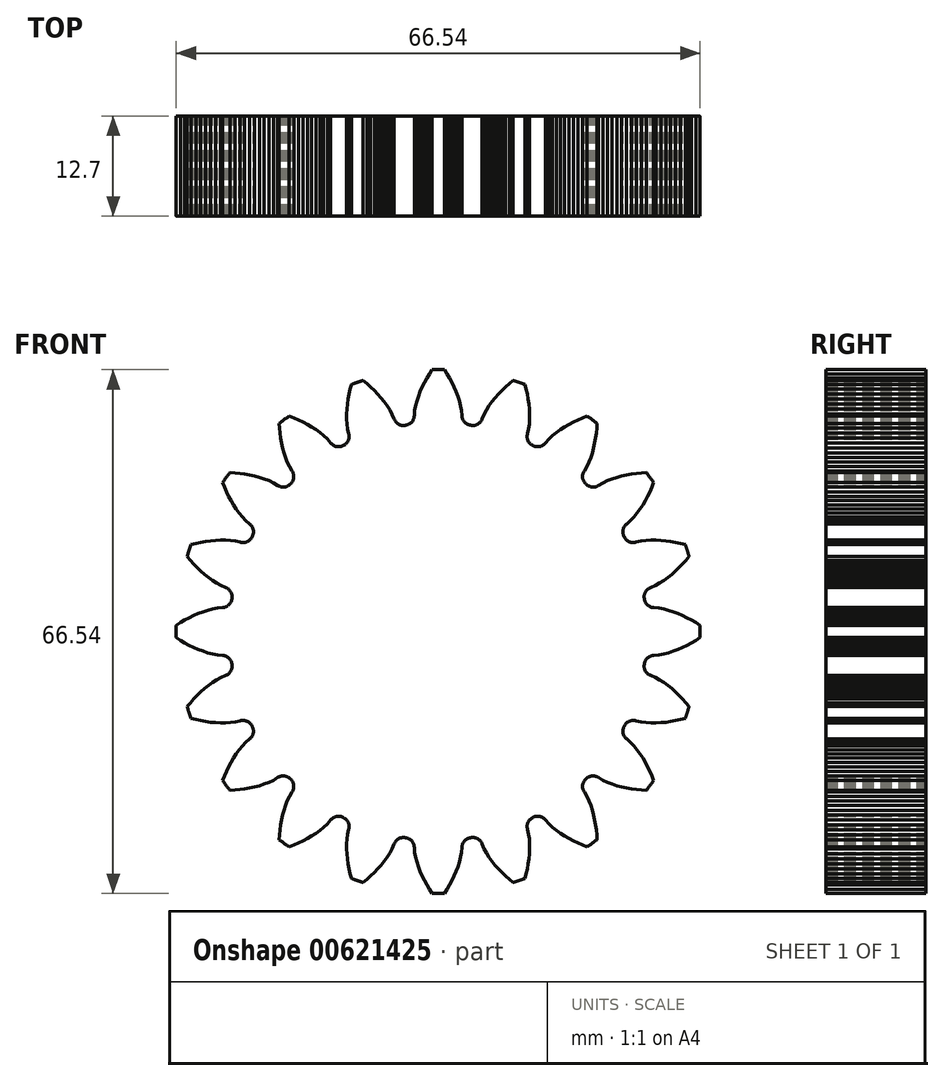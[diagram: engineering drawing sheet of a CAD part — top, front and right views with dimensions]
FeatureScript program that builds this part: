
annotation { "Feature Type Name" : "Feature", "Feature Type Description" : "" }
export const myFeature = defineFeature(function(context is Context, id is Id, definition is map)
    precondition{}
    {
        {
            var Q0;
            Q0=qCreatedBy(makeId("Front.planeOp"),FACE);
            var sketch = newSketch(context, id + "F0", { "sketchPlane" : qUnion([Q0])});
            skLineSegment(sketch, "E0", {"start": v(3.03, 27.4) * mm, "end": v(2.97, 28.04) * mm});
            skLineSegment(sketch, "E1", {"start": v(2.97, 28.04) * mm, "end": v(2.86, 28.66) * mm});
            skLineSegment(sketch, "E2", {"start": v(2.86, 28.66) * mm, "end": v(2.7, 29.28) * mm});
            skLineSegment(sketch, "E3", {"start": v(2.7, 29.28) * mm, "end": v(2.5, 29.88) * mm});
            skLineSegment(sketch, "E4", {"start": v(2.5, 29.88) * mm, "end": v(2.28, 30.47) * mm});
            skLineSegment(sketch, "E5", {"start": v(2.28, 30.47) * mm, "end": v(2.02, 31.05) * mm});
            skLineSegment(sketch, "E6", {"start": v(2.02, 31.05) * mm, "end": v(1.74, 31.62) * mm});
            skLineSegment(sketch, "E7", {"start": v(1.74, 31.62) * mm, "end": v(1.44, 32.18) * mm});
            skLineSegment(sketch, "E8", {"start": v(1.44, 32.18) * mm, "end": v(1.12, 32.73) * mm});
            skLineSegment(sketch, "E9", {"start": v(1.12, 32.73) * mm, "end": v(0.78, 33.26) * mm});
            skLineSegment(sketch, "E10", {"start": v(-3.03, 27.4) * mm, "end": v(-2.97, 28.04) * mm});
            skLineSegment(sketch, "E11", {"start": v(-2.97, 28.04) * mm, "end": v(-2.86, 28.66) * mm});
            skLineSegment(sketch, "E12", {"start": v(-2.86, 28.66) * mm, "end": v(-2.7, 29.28) * mm});
            skLineSegment(sketch, "E13", {"start": v(-2.7, 29.28) * mm, "end": v(-2.5, 29.88) * mm});
            skLineSegment(sketch, "E14", {"start": v(-2.5, 29.88) * mm, "end": v(-2.28, 30.47) * mm});
            skLineSegment(sketch, "E15", {"start": v(-2.28, 30.47) * mm, "end": v(-2.02, 31.05) * mm});
            skLineSegment(sketch, "E16", {"start": v(-2.02, 31.05) * mm, "end": v(-1.74, 31.62) * mm});
            skLineSegment(sketch, "E17", {"start": v(-1.74, 31.62) * mm, "end": v(-1.44, 32.18) * mm});
            skLineSegment(sketch, "E18", {"start": v(-1.44, 32.18) * mm, "end": v(-1.12, 32.73) * mm});
            skLineSegment(sketch, "E19", {"start": v(-1.12, 32.73) * mm, "end": v(-0.78, 33.26) * mm});
            skArc(sketch, "E20", {"start": v(-4.08, 26.2) * mm, "mid": v(-4.15, 26.2) * mm, "end": v(-4.22, 26.19) * mm});
            skArc(sketch, "E21", {"start": v(-4.08, 26.2) * mm, "mid": v(-3.34, 26.62) * mm, "end": v(-3.03, 27.4) * mm});
            skArc(sketch, "E22", {"start": v(3.03, 27.4) * mm, "mid": v(3.34, 26.62) * mm, "end": v(4.08, 26.2) * mm});
            skArc(sketch, "E23", {"start": v(0.78, 33.26) * mm, "mid": v(0, 33.27) * mm, "end": v(-0.78, 33.26) * mm});
            skArc(sketch, "E24", {"start": v(-11.98, 23.66) * mm, "mid": v(-12.04, 23.63) * mm, "end": v(-12.1, 23.6) * mm});
            skArc(sketch, "E25", {"start": v(-18.7, 18.8) * mm, "mid": v(-18.76, 18.76) * mm, "end": v(-18.8, 18.7) * mm});
            skArc(sketch, "E26", {"start": v(-23.6, 12.1) * mm, "mid": v(-23.63, 12.04) * mm, "end": v(-23.66, 11.98) * mm});
            skArc(sketch, "E27", {"start": v(-26.19, 4.22) * mm, "mid": v(-26.2, 4.15) * mm, "end": v(-26.2, 4.08) * mm});
            skArc(sketch, "E28", {"start": v(-26.2, -4.08) * mm, "mid": v(-26.2, -4.15) * mm, "end": v(-26.19, -4.22) * mm});
            skLineSegment(sketch, "E29", {"start": v(-5.59, 27) * mm, "end": v(-5.84, 27.59) * mm});
            skLineSegment(sketch, "E30", {"start": v(-5.84, 27.59) * mm, "end": v(-6.14, 28.14) * mm});
            skLineSegment(sketch, "E31", {"start": v(-6.14, 28.14) * mm, "end": v(-6.48, 28.68) * mm});
            skLineSegment(sketch, "E32", {"start": v(-6.48, 28.68) * mm, "end": v(-6.85, 29.2) * mm});
            skLineSegment(sketch, "E33", {"start": v(-6.85, 29.2) * mm, "end": v(-7.25, 29.69) * mm});
            skLineSegment(sketch, "E34", {"start": v(-7.25, 29.69) * mm, "end": v(-7.67, 30.16) * mm});
            skLineSegment(sketch, "E35", {"start": v(-7.67, 30.16) * mm, "end": v(-8.11, 30.62) * mm});
            skLineSegment(sketch, "E36", {"start": v(-8.11, 30.62) * mm, "end": v(-8.57, 31.05) * mm});
            skLineSegment(sketch, "E37", {"start": v(-8.57, 31.05) * mm, "end": v(-9.05, 31.47) * mm});
            skLineSegment(sketch, "E38", {"start": v(-9.05, 31.47) * mm, "end": v(-9.54, 31.88) * mm});
            skLineSegment(sketch, "E39", {"start": v(-13.66, 23.96) * mm, "end": v(-14.08, 24.43) * mm});
            skLineSegment(sketch, "E40", {"start": v(-14.08, 24.43) * mm, "end": v(-14.54, 24.87) * mm});
            skLineSegment(sketch, "E41", {"start": v(-14.54, 24.87) * mm, "end": v(-15.03, 25.27) * mm});
            skLineSegment(sketch, "E42", {"start": v(-15.03, 25.27) * mm, "end": v(-15.54, 25.65) * mm});
            skLineSegment(sketch, "E43", {"start": v(-15.54, 25.65) * mm, "end": v(-16.07, 26) * mm});
            skLineSegment(sketch, "E44", {"start": v(-16.07, 26) * mm, "end": v(-16.62, 26.31) * mm});
            skLineSegment(sketch, "E45", {"start": v(-16.62, 26.31) * mm, "end": v(-17.18, 26.61) * mm});
            skLineSegment(sketch, "E46", {"start": v(-17.18, 26.61) * mm, "end": v(-17.75, 26.89) * mm});
            skLineSegment(sketch, "E47", {"start": v(-17.75, 26.89) * mm, "end": v(-18.33, 27.14) * mm});
            skLineSegment(sketch, "E48", {"start": v(-18.33, 27.14) * mm, "end": v(-18.92, 27.37) * mm});
            skArc(sketch, "E49", {"start": v(-23.66, -11.98) * mm, "mid": v(-23.63, -12.04) * mm, "end": v(-23.6, -12.1) * mm});
            skArc(sketch, "E50", {"start": v(-18.8, -18.7) * mm, "mid": v(-18.76, -18.76) * mm, "end": v(-18.7, -18.8) * mm});
            skArc(sketch, "E51", {"start": v(-12.1, -23.6) * mm, "mid": v(-12.04, -23.63) * mm, "end": v(-11.98, -23.66) * mm});
            skArc(sketch, "E52", {"start": v(-4.22, -26.19) * mm, "mid": v(-4.15, -26.2) * mm, "end": v(-4.08, -26.2) * mm});
            skLineSegment(sketch, "E53", {"start": v(-20.4, 18.56) * mm, "end": v(-20.94, 18.89) * mm});
            skLineSegment(sketch, "E54", {"start": v(-20.94, 18.89) * mm, "end": v(-21.5, 19.16) * mm});
            skLineSegment(sketch, "E55", {"start": v(-21.5, 19.16) * mm, "end": v(-22.1, 19.4) * mm});
            skLineSegment(sketch, "E56", {"start": v(-22.1, 19.4) * mm, "end": v(-22.7, 19.59) * mm});
            skLineSegment(sketch, "E57", {"start": v(-22.7, 19.59) * mm, "end": v(-23.32, 19.75) * mm});
            skLineSegment(sketch, "E58", {"start": v(-23.32, 19.75) * mm, "end": v(-23.93, 19.89) * mm});
            skLineSegment(sketch, "E59", {"start": v(-23.93, 19.89) * mm, "end": v(-24.56, 20) * mm});
            skLineSegment(sketch, "E60", {"start": v(-24.56, 20) * mm, "end": v(-25.19, 20.08) * mm});
            skLineSegment(sketch, "E61", {"start": v(-25.19, 20.08) * mm, "end": v(-25.82, 20.15) * mm});
            skLineSegment(sketch, "E62", {"start": v(-25.82, 20.15) * mm, "end": v(-26.45, 20.19) * mm});
            skLineSegment(sketch, "E63", {"start": v(-25.13, 11.35) * mm, "end": v(-25.75, 11.5) * mm});
            skLineSegment(sketch, "E64", {"start": v(-25.75, 11.5) * mm, "end": v(-26.38, 11.58) * mm});
            skLineSegment(sketch, "E65", {"start": v(-26.38, 11.58) * mm, "end": v(-27.01, 11.61) * mm});
            skLineSegment(sketch, "E66", {"start": v(-27.01, 11.61) * mm, "end": v(-27.64, 11.61) * mm});
            skLineSegment(sketch, "E67", {"start": v(-27.64, 11.61) * mm, "end": v(-28.28, 11.58) * mm});
            skLineSegment(sketch, "E68", {"start": v(-28.28, 11.58) * mm, "end": v(-28.9, 11.52) * mm});
            skLineSegment(sketch, "E69", {"start": v(-28.9, 11.52) * mm, "end": v(-29.54, 11.43) * mm});
            skLineSegment(sketch, "E70", {"start": v(-29.54, 11.43) * mm, "end": v(-30.16, 11.32) * mm});
            skLineSegment(sketch, "E71", {"start": v(-30.16, 11.32) * mm, "end": v(-30.78, 11.18) * mm});
            skLineSegment(sketch, "E72", {"start": v(-30.78, 11.18) * mm, "end": v(-31.4, 11.02) * mm});
            skLineSegment(sketch, "E73", {"start": v(-27.4, 3.03) * mm, "end": v(-28.04, 2.97) * mm});
            skLineSegment(sketch, "E74", {"start": v(-28.04, 2.97) * mm, "end": v(-28.66, 2.86) * mm});
            skLineSegment(sketch, "E75", {"start": v(-28.66, 2.86) * mm, "end": v(-29.28, 2.7) * mm});
            skLineSegment(sketch, "E76", {"start": v(-29.28, 2.7) * mm, "end": v(-29.88, 2.5) * mm});
            skLineSegment(sketch, "E77", {"start": v(-29.88, 2.5) * mm, "end": v(-30.47, 2.28) * mm});
            skLineSegment(sketch, "E78", {"start": v(-30.47, 2.28) * mm, "end": v(-31.05, 2.02) * mm});
            skLineSegment(sketch, "E79", {"start": v(-31.05, 2.02) * mm, "end": v(-31.62, 1.74) * mm});
            skLineSegment(sketch, "E80", {"start": v(-31.62, 1.74) * mm, "end": v(-32.18, 1.44) * mm});
            skLineSegment(sketch, "E81", {"start": v(-32.18, 1.44) * mm, "end": v(-32.73, 1.12) * mm});
            skLineSegment(sketch, "E82", {"start": v(-32.73, 1.12) * mm, "end": v(-33.26, 0.78) * mm});
            skLineSegment(sketch, "E83", {"start": v(-27, -5.59) * mm, "end": v(-27.59, -5.84) * mm});
            skLineSegment(sketch, "E84", {"start": v(-27.59, -5.84) * mm, "end": v(-28.14, -6.14) * mm});
            skLineSegment(sketch, "E85", {"start": v(-28.14, -6.14) * mm, "end": v(-28.68, -6.48) * mm});
            skLineSegment(sketch, "E86", {"start": v(-28.68, -6.48) * mm, "end": v(-29.2, -6.85) * mm});
            skLineSegment(sketch, "E87", {"start": v(-29.2, -6.85) * mm, "end": v(-29.69, -7.25) * mm});
            skLineSegment(sketch, "E88", {"start": v(-29.69, -7.25) * mm, "end": v(-30.16, -7.67) * mm});
            skLineSegment(sketch, "E89", {"start": v(-30.16, -7.67) * mm, "end": v(-30.62, -8.11) * mm});
            skLineSegment(sketch, "E90", {"start": v(-30.62, -8.11) * mm, "end": v(-31.05, -8.57) * mm});
            skLineSegment(sketch, "E91", {"start": v(-31.05, -8.57) * mm, "end": v(-31.47, -9.05) * mm});
            skLineSegment(sketch, "E92", {"start": v(-31.47, -9.05) * mm, "end": v(-31.88, -9.54) * mm});
            skArc(sketch, "E93", {"start": v(4.08, -26.2) * mm, "mid": v(4.15, -26.2) * mm, "end": v(4.22, -26.19) * mm});
            skArc(sketch, "E94", {"start": v(11.98, -23.66) * mm, "mid": v(12.04, -23.63) * mm, "end": v(12.1, -23.6) * mm});
            skArc(sketch, "E95", {"start": v(18.7, -18.8) * mm, "mid": v(18.76, -18.76) * mm, "end": v(18.8, -18.7) * mm});
            skArc(sketch, "E96", {"start": v(23.6, -12.1) * mm, "mid": v(23.63, -12.04) * mm, "end": v(23.66, -11.98) * mm});
            skLineSegment(sketch, "E97", {"start": v(-23.96, -13.66) * mm, "end": v(-24.43, -14.08) * mm});
            skLineSegment(sketch, "E98", {"start": v(-24.43, -14.08) * mm, "end": v(-24.87, -14.54) * mm});
            skLineSegment(sketch, "E99", {"start": v(-24.87, -14.54) * mm, "end": v(-25.27, -15.03) * mm});
            skLineSegment(sketch, "E100", {"start": v(-25.27, -15.03) * mm, "end": v(-25.65, -15.54) * mm});
            skLineSegment(sketch, "E101", {"start": v(-25.65, -15.54) * mm, "end": v(-26, -16.07) * mm});
            skLineSegment(sketch, "E102", {"start": v(-26, -16.07) * mm, "end": v(-26.31, -16.62) * mm});
            skLineSegment(sketch, "E103", {"start": v(-26.31, -16.62) * mm, "end": v(-26.61, -17.18) * mm});
            skLineSegment(sketch, "E104", {"start": v(-26.61, -17.18) * mm, "end": v(-26.89, -17.75) * mm});
            skLineSegment(sketch, "E105", {"start": v(-26.89, -17.75) * mm, "end": v(-27.14, -18.33) * mm});
            skLineSegment(sketch, "E106", {"start": v(-27.14, -18.33) * mm, "end": v(-27.37, -18.92) * mm});
            skLineSegment(sketch, "E107", {"start": v(-18.56, -20.4) * mm, "end": v(-18.89, -20.94) * mm});
            skLineSegment(sketch, "E108", {"start": v(-18.89, -20.94) * mm, "end": v(-19.16, -21.5) * mm});
            skLineSegment(sketch, "E109", {"start": v(-19.16, -21.5) * mm, "end": v(-19.4, -22.1) * mm});
            skLineSegment(sketch, "E110", {"start": v(-19.4, -22.1) * mm, "end": v(-19.59, -22.7) * mm});
            skLineSegment(sketch, "E111", {"start": v(-19.59, -22.7) * mm, "end": v(-19.75, -23.32) * mm});
            skLineSegment(sketch, "E112", {"start": v(-19.75, -23.32) * mm, "end": v(-19.89, -23.93) * mm});
            skLineSegment(sketch, "E113", {"start": v(-19.89, -23.93) * mm, "end": v(-20, -24.56) * mm});
            skLineSegment(sketch, "E114", {"start": v(-20, -24.56) * mm, "end": v(-20.08, -25.19) * mm});
            skLineSegment(sketch, "E115", {"start": v(-20.08, -25.19) * mm, "end": v(-20.15, -25.82) * mm});
            skLineSegment(sketch, "E116", {"start": v(-20.15, -25.82) * mm, "end": v(-20.19, -26.45) * mm});
            skLineSegment(sketch, "E117", {"start": v(-11.35, -25.13) * mm, "end": v(-11.5, -25.75) * mm});
            skLineSegment(sketch, "E118", {"start": v(-11.5, -25.75) * mm, "end": v(-11.58, -26.38) * mm});
            skLineSegment(sketch, "E119", {"start": v(-11.58, -26.38) * mm, "end": v(-11.61, -27.01) * mm});
            skLineSegment(sketch, "E120", {"start": v(-11.61, -27.01) * mm, "end": v(-11.61, -27.64) * mm});
            skLineSegment(sketch, "E121", {"start": v(-11.61, -27.64) * mm, "end": v(-11.58, -28.28) * mm});
            skLineSegment(sketch, "E122", {"start": v(-11.58, -28.28) * mm, "end": v(-11.52, -28.9) * mm});
            skLineSegment(sketch, "E123", {"start": v(-11.52, -28.9) * mm, "end": v(-11.43, -29.54) * mm});
            skLineSegment(sketch, "E124", {"start": v(-11.43, -29.54) * mm, "end": v(-11.32, -30.16) * mm});
            skLineSegment(sketch, "E125", {"start": v(-11.32, -30.16) * mm, "end": v(-11.18, -30.78) * mm});
            skLineSegment(sketch, "E126", {"start": v(-11.18, -30.78) * mm, "end": v(-11.02, -31.4) * mm});
            skLineSegment(sketch, "E127", {"start": v(-3.03, -27.4) * mm, "end": v(-2.97, -28.04) * mm});
            skLineSegment(sketch, "E128", {"start": v(-2.97, -28.04) * mm, "end": v(-2.86, -28.66) * mm});
            skLineSegment(sketch, "E129", {"start": v(-2.86, -28.66) * mm, "end": v(-2.7, -29.28) * mm});
            skLineSegment(sketch, "E130", {"start": v(-2.7, -29.28) * mm, "end": v(-2.5, -29.88) * mm});
            skLineSegment(sketch, "E131", {"start": v(-2.5, -29.88) * mm, "end": v(-2.28, -30.47) * mm});
            skLineSegment(sketch, "E132", {"start": v(-2.28, -30.47) * mm, "end": v(-2.02, -31.05) * mm});
            skLineSegment(sketch, "E133", {"start": v(-2.02, -31.05) * mm, "end": v(-1.74, -31.62) * mm});
            skLineSegment(sketch, "E134", {"start": v(-1.74, -31.62) * mm, "end": v(-1.44, -32.18) * mm});
            skLineSegment(sketch, "E135", {"start": v(-1.44, -32.18) * mm, "end": v(-1.12, -32.73) * mm});
            skLineSegment(sketch, "E136", {"start": v(-1.12, -32.73) * mm, "end": v(-0.78, -33.26) * mm});
            skArc(sketch, "E137", {"start": v(26.19, -4.22) * mm, "mid": v(26.2, -4.15) * mm, "end": v(26.2, -4.08) * mm});
            skArc(sketch, "E138", {"start": v(26.2, 4.08) * mm, "mid": v(26.2, 4.15) * mm, "end": v(26.19, 4.22) * mm});
            skArc(sketch, "E139", {"start": v(23.66, 11.98) * mm, "mid": v(23.63, 12.04) * mm, "end": v(23.6, 12.1) * mm});
            skArc(sketch, "E140", {"start": v(18.8, 18.7) * mm, "mid": v(18.76, 18.76) * mm, "end": v(18.7, 18.8) * mm});
            skLineSegment(sketch, "E141", {"start": v(5.59, -27) * mm, "end": v(5.84, -27.59) * mm});
            skLineSegment(sketch, "E142", {"start": v(5.84, -27.59) * mm, "end": v(6.14, -28.14) * mm});
            skLineSegment(sketch, "E143", {"start": v(6.14, -28.14) * mm, "end": v(6.48, -28.68) * mm});
            skLineSegment(sketch, "E144", {"start": v(6.48, -28.68) * mm, "end": v(6.85, -29.2) * mm});
            skLineSegment(sketch, "E145", {"start": v(6.85, -29.2) * mm, "end": v(7.25, -29.69) * mm});
            skLineSegment(sketch, "E146", {"start": v(7.25, -29.69) * mm, "end": v(7.67, -30.16) * mm});
            skLineSegment(sketch, "E147", {"start": v(7.67, -30.16) * mm, "end": v(8.11, -30.62) * mm});
            skLineSegment(sketch, "E148", {"start": v(8.11, -30.62) * mm, "end": v(8.57, -31.05) * mm});
            skLineSegment(sketch, "E149", {"start": v(8.57, -31.05) * mm, "end": v(9.05, -31.47) * mm});
            skLineSegment(sketch, "E150", {"start": v(9.05, -31.47) * mm, "end": v(9.54, -31.88) * mm});
            skLineSegment(sketch, "E151", {"start": v(13.66, -23.96) * mm, "end": v(14.08, -24.43) * mm});
            skLineSegment(sketch, "E152", {"start": v(14.08, -24.43) * mm, "end": v(14.54, -24.87) * mm});
            skLineSegment(sketch, "E153", {"start": v(14.54, -24.87) * mm, "end": v(15.03, -25.27) * mm});
            skLineSegment(sketch, "E154", {"start": v(15.03, -25.27) * mm, "end": v(15.54, -25.65) * mm});
            skLineSegment(sketch, "E155", {"start": v(15.54, -25.65) * mm, "end": v(16.07, -26) * mm});
            skLineSegment(sketch, "E156", {"start": v(16.07, -26) * mm, "end": v(16.62, -26.31) * mm});
            skLineSegment(sketch, "E157", {"start": v(16.62, -26.31) * mm, "end": v(17.18, -26.61) * mm});
            skLineSegment(sketch, "E158", {"start": v(17.18, -26.61) * mm, "end": v(17.75, -26.89) * mm});
            skLineSegment(sketch, "E159", {"start": v(17.75, -26.89) * mm, "end": v(18.33, -27.14) * mm});
            skLineSegment(sketch, "E160", {"start": v(18.33, -27.14) * mm, "end": v(18.92, -27.37) * mm});
            skLineSegment(sketch, "E161", {"start": v(20.4, -18.56) * mm, "end": v(20.94, -18.89) * mm});
            skLineSegment(sketch, "E162", {"start": v(20.94, -18.89) * mm, "end": v(21.5, -19.16) * mm});
            skLineSegment(sketch, "E163", {"start": v(21.5, -19.16) * mm, "end": v(22.1, -19.4) * mm});
            skLineSegment(sketch, "E164", {"start": v(22.1, -19.4) * mm, "end": v(22.7, -19.59) * mm});
            skLineSegment(sketch, "E165", {"start": v(22.7, -19.59) * mm, "end": v(23.32, -19.75) * mm});
            skLineSegment(sketch, "E166", {"start": v(23.32, -19.75) * mm, "end": v(23.93, -19.89) * mm});
            skLineSegment(sketch, "E167", {"start": v(23.93, -19.89) * mm, "end": v(24.56, -20) * mm});
            skLineSegment(sketch, "E168", {"start": v(24.56, -20) * mm, "end": v(25.19, -20.08) * mm});
            skLineSegment(sketch, "E169", {"start": v(25.19, -20.08) * mm, "end": v(25.82, -20.15) * mm});
            skLineSegment(sketch, "E170", {"start": v(25.82, -20.15) * mm, "end": v(26.45, -20.19) * mm});
            skLineSegment(sketch, "E171", {"start": v(25.13, -11.35) * mm, "end": v(25.75, -11.5) * mm});
            skLineSegment(sketch, "E172", {"start": v(25.75, -11.5) * mm, "end": v(26.38, -11.58) * mm});
            skLineSegment(sketch, "E173", {"start": v(26.38, -11.58) * mm, "end": v(27.01, -11.61) * mm});
            skLineSegment(sketch, "E174", {"start": v(27.01, -11.61) * mm, "end": v(27.64, -11.61) * mm});
            skLineSegment(sketch, "E175", {"start": v(27.64, -11.61) * mm, "end": v(28.28, -11.58) * mm});
            skLineSegment(sketch, "E176", {"start": v(28.28, -11.58) * mm, "end": v(28.9, -11.52) * mm});
            skLineSegment(sketch, "E177", {"start": v(28.9, -11.52) * mm, "end": v(29.54, -11.43) * mm});
            skLineSegment(sketch, "E178", {"start": v(29.54, -11.43) * mm, "end": v(30.16, -11.32) * mm});
            skLineSegment(sketch, "E179", {"start": v(30.16, -11.32) * mm, "end": v(30.78, -11.18) * mm});
            skLineSegment(sketch, "E180", {"start": v(30.78, -11.18) * mm, "end": v(31.4, -11.02) * mm});
            skArc(sketch, "E181", {"start": v(12.1, 23.6) * mm, "mid": v(12.04, 23.63) * mm, "end": v(11.98, 23.66) * mm});
            skArc(sketch, "E182", {"start": v(4.22, 26.19) * mm, "mid": v(4.15, 26.2) * mm, "end": v(4.08, 26.2) * mm});
            skArc(sketch, "E183", {"start": v(-11.98, 23.66) * mm, "mid": v(-11.4, 24.28) * mm, "end": v(-11.35, 25.13) * mm});
            skArc(sketch, "E184", {"start": v(-18.7, 18.8) * mm, "mid": v(-18.35, 19.57) * mm, "end": v(-18.56, 20.4) * mm});
            skLineSegment(sketch, "E185", {"start": v(27.4, -3.03) * mm, "end": v(28.04, -2.97) * mm});
            skLineSegment(sketch, "E186", {"start": v(28.04, -2.97) * mm, "end": v(28.66, -2.86) * mm});
            skLineSegment(sketch, "E187", {"start": v(28.66, -2.86) * mm, "end": v(29.28, -2.7) * mm});
            skLineSegment(sketch, "E188", {"start": v(29.28, -2.7) * mm, "end": v(29.88, -2.5) * mm});
            skLineSegment(sketch, "E189", {"start": v(29.88, -2.5) * mm, "end": v(30.47, -2.28) * mm});
            skLineSegment(sketch, "E190", {"start": v(30.47, -2.28) * mm, "end": v(31.05, -2.02) * mm});
            skLineSegment(sketch, "E191", {"start": v(31.05, -2.02) * mm, "end": v(31.62, -1.74) * mm});
            skLineSegment(sketch, "E192", {"start": v(31.62, -1.74) * mm, "end": v(32.18, -1.44) * mm});
            skLineSegment(sketch, "E193", {"start": v(32.18, -1.44) * mm, "end": v(32.73, -1.12) * mm});
            skLineSegment(sketch, "E194", {"start": v(32.73, -1.12) * mm, "end": v(33.26, -0.78) * mm});
            skLineSegment(sketch, "E195", {"start": v(27, 5.59) * mm, "end": v(27.59, 5.84) * mm});
            skLineSegment(sketch, "E196", {"start": v(27.59, 5.84) * mm, "end": v(28.14, 6.14) * mm});
            skLineSegment(sketch, "E197", {"start": v(28.14, 6.14) * mm, "end": v(28.68, 6.48) * mm});
            skLineSegment(sketch, "E198", {"start": v(28.68, 6.48) * mm, "end": v(29.2, 6.85) * mm});
            skLineSegment(sketch, "E199", {"start": v(29.2, 6.85) * mm, "end": v(29.69, 7.25) * mm});
            skLineSegment(sketch, "E200", {"start": v(29.69, 7.25) * mm, "end": v(30.16, 7.67) * mm});
            skLineSegment(sketch, "E201", {"start": v(30.16, 7.67) * mm, "end": v(30.62, 8.11) * mm});
            skLineSegment(sketch, "E202", {"start": v(30.62, 8.11) * mm, "end": v(31.05, 8.57) * mm});
            skLineSegment(sketch, "E203", {"start": v(31.05, 8.57) * mm, "end": v(31.47, 9.05) * mm});
            skLineSegment(sketch, "E204", {"start": v(31.47, 9.05) * mm, "end": v(31.88, 9.54) * mm});
            skLineSegment(sketch, "E205", {"start": v(23.96, 13.66) * mm, "end": v(24.43, 14.08) * mm});
            skLineSegment(sketch, "E206", {"start": v(24.43, 14.08) * mm, "end": v(24.87, 14.54) * mm});
            skLineSegment(sketch, "E207", {"start": v(24.87, 14.54) * mm, "end": v(25.27, 15.03) * mm});
            skLineSegment(sketch, "E208", {"start": v(25.27, 15.03) * mm, "end": v(25.65, 15.54) * mm});
            skLineSegment(sketch, "E209", {"start": v(25.65, 15.54) * mm, "end": v(26, 16.07) * mm});
            skLineSegment(sketch, "E210", {"start": v(26, 16.07) * mm, "end": v(26.31, 16.62) * mm});
            skLineSegment(sketch, "E211", {"start": v(26.31, 16.62) * mm, "end": v(26.61, 17.18) * mm});
            skLineSegment(sketch, "E212", {"start": v(26.61, 17.18) * mm, "end": v(26.89, 17.75) * mm});
            skLineSegment(sketch, "E213", {"start": v(26.89, 17.75) * mm, "end": v(27.14, 18.33) * mm});
            skLineSegment(sketch, "E214", {"start": v(27.14, 18.33) * mm, "end": v(27.37, 18.92) * mm});
            skLineSegment(sketch, "E215", {"start": v(18.56, 20.4) * mm, "end": v(18.89, 20.94) * mm});
            skLineSegment(sketch, "E216", {"start": v(18.89, 20.94) * mm, "end": v(19.16, 21.5) * mm});
            skLineSegment(sketch, "E217", {"start": v(19.16, 21.5) * mm, "end": v(19.4, 22.1) * mm});
            skLineSegment(sketch, "E218", {"start": v(19.4, 22.1) * mm, "end": v(19.59, 22.7) * mm});
            skLineSegment(sketch, "E219", {"start": v(19.59, 22.7) * mm, "end": v(19.75, 23.32) * mm});
            skLineSegment(sketch, "E220", {"start": v(19.75, 23.32) * mm, "end": v(19.89, 23.93) * mm});
            skLineSegment(sketch, "E221", {"start": v(19.89, 23.93) * mm, "end": v(20, 24.56) * mm});
            skLineSegment(sketch, "E222", {"start": v(20, 24.56) * mm, "end": v(20.08, 25.19) * mm});
            skLineSegment(sketch, "E223", {"start": v(20.08, 25.19) * mm, "end": v(20.15, 25.82) * mm});
            skLineSegment(sketch, "E224", {"start": v(20.15, 25.82) * mm, "end": v(20.19, 26.45) * mm});
            skArc(sketch, "E225", {"start": v(-23.6, 12.1) * mm, "mid": v(-23.5, 12.94) * mm, "end": v(-23.96, 13.66) * mm});
            skArc(sketch, "E226", {"start": v(-26.19, 4.22) * mm, "mid": v(-26.35, 5.05) * mm, "end": v(-27, 5.59) * mm});
            skArc(sketch, "E227", {"start": v(-26.2, -4.08) * mm, "mid": v(-26.62, -3.34) * mm, "end": v(-27.4, -3.03) * mm});
            skArc(sketch, "E228", {"start": v(-23.66, -11.98) * mm, "mid": v(-24.28, -11.4) * mm, "end": v(-25.13, -11.35) * mm});
            skLineSegment(sketch, "E229", {"start": v(11.35, 25.13) * mm, "end": v(11.5, 25.75) * mm});
            skLineSegment(sketch, "E230", {"start": v(11.5, 25.75) * mm, "end": v(11.58, 26.38) * mm});
            skLineSegment(sketch, "E231", {"start": v(11.58, 26.38) * mm, "end": v(11.61, 27.01) * mm});
            skLineSegment(sketch, "E232", {"start": v(11.61, 27.01) * mm, "end": v(11.61, 27.64) * mm});
            skLineSegment(sketch, "E233", {"start": v(11.61, 27.64) * mm, "end": v(11.58, 28.28) * mm});
            skLineSegment(sketch, "E234", {"start": v(11.58, 28.28) * mm, "end": v(11.52, 28.9) * mm});
            skLineSegment(sketch, "E235", {"start": v(11.52, 28.9) * mm, "end": v(11.43, 29.54) * mm});
            skLineSegment(sketch, "E236", {"start": v(11.43, 29.54) * mm, "end": v(11.32, 30.16) * mm});
            skLineSegment(sketch, "E237", {"start": v(11.32, 30.16) * mm, "end": v(11.18, 30.78) * mm});
            skLineSegment(sketch, "E238", {"start": v(11.18, 30.78) * mm, "end": v(11.02, 31.4) * mm});
            skLineSegment(sketch, "E239", {"start": v(-11.35, 25.13) * mm, "end": v(-11.5, 25.75) * mm});
            skLineSegment(sketch, "E240", {"start": v(-11.5, 25.75) * mm, "end": v(-11.58, 26.38) * mm});
            skLineSegment(sketch, "E241", {"start": v(-11.58, 26.38) * mm, "end": v(-11.61, 27.01) * mm});
            skLineSegment(sketch, "E242", {"start": v(-11.61, 27.01) * mm, "end": v(-11.61, 27.64) * mm});
            skLineSegment(sketch, "E243", {"start": v(-11.61, 27.64) * mm, "end": v(-11.58, 28.28) * mm});
            skLineSegment(sketch, "E244", {"start": v(-11.58, 28.28) * mm, "end": v(-11.52, 28.9) * mm});
            skLineSegment(sketch, "E245", {"start": v(-11.52, 28.9) * mm, "end": v(-11.43, 29.54) * mm});
            skLineSegment(sketch, "E246", {"start": v(-11.43, 29.54) * mm, "end": v(-11.32, 30.16) * mm});
            skLineSegment(sketch, "E247", {"start": v(-11.32, 30.16) * mm, "end": v(-11.18, 30.78) * mm});
            skLineSegment(sketch, "E248", {"start": v(-11.18, 30.78) * mm, "end": v(-11.02, 31.4) * mm});
            skLineSegment(sketch, "E249", {"start": v(-18.56, 20.4) * mm, "end": v(-18.89, 20.94) * mm});
            skLineSegment(sketch, "E250", {"start": v(-18.89, 20.94) * mm, "end": v(-19.16, 21.5) * mm});
            skLineSegment(sketch, "E251", {"start": v(-19.16, 21.5) * mm, "end": v(-19.4, 22.1) * mm});
            skLineSegment(sketch, "E252", {"start": v(-19.4, 22.1) * mm, "end": v(-19.59, 22.7) * mm});
            skLineSegment(sketch, "E253", {"start": v(-19.59, 22.7) * mm, "end": v(-19.75, 23.32) * mm});
            skLineSegment(sketch, "E254", {"start": v(-19.75, 23.32) * mm, "end": v(-19.89, 23.93) * mm});
            skLineSegment(sketch, "E255", {"start": v(-19.89, 23.93) * mm, "end": v(-20, 24.56) * mm});
            skLineSegment(sketch, "E256", {"start": v(-20, 24.56) * mm, "end": v(-20.08, 25.19) * mm});
            skLineSegment(sketch, "E257", {"start": v(-20.08, 25.19) * mm, "end": v(-20.15, 25.82) * mm});
            skLineSegment(sketch, "E258", {"start": v(-20.15, 25.82) * mm, "end": v(-20.19, 26.45) * mm});
            skLineSegment(sketch, "E259", {"start": v(-23.96, 13.66) * mm, "end": v(-24.43, 14.08) * mm});
            skLineSegment(sketch, "E260", {"start": v(-24.43, 14.08) * mm, "end": v(-24.87, 14.54) * mm});
            skLineSegment(sketch, "E261", {"start": v(-24.87, 14.54) * mm, "end": v(-25.27, 15.03) * mm});
            skLineSegment(sketch, "E262", {"start": v(-25.27, 15.03) * mm, "end": v(-25.65, 15.54) * mm});
            skLineSegment(sketch, "E263", {"start": v(-25.65, 15.54) * mm, "end": v(-26, 16.07) * mm});
            skLineSegment(sketch, "E264", {"start": v(-26, 16.07) * mm, "end": v(-26.31, 16.62) * mm});
            skLineSegment(sketch, "E265", {"start": v(-26.31, 16.62) * mm, "end": v(-26.61, 17.18) * mm});
            skLineSegment(sketch, "E266", {"start": v(-26.61, 17.18) * mm, "end": v(-26.89, 17.75) * mm});
            skLineSegment(sketch, "E267", {"start": v(-26.89, 17.75) * mm, "end": v(-27.14, 18.33) * mm});
            skLineSegment(sketch, "E268", {"start": v(-27.14, 18.33) * mm, "end": v(-27.37, 18.92) * mm});
            skArc(sketch, "E269", {"start": v(-18.8, -18.7) * mm, "mid": v(-19.57, -18.35) * mm, "end": v(-20.4, -18.56) * mm});
            skArc(sketch, "E270", {"start": v(-12.1, -23.6) * mm, "mid": v(-12.94, -23.5) * mm, "end": v(-13.66, -23.96) * mm});
            skArc(sketch, "E271", {"start": v(-4.22, -26.19) * mm, "mid": v(-5.05, -26.35) * mm, "end": v(-5.59, -27) * mm});
            skArc(sketch, "E272", {"start": v(4.08, -26.2) * mm, "mid": v(3.34, -26.62) * mm, "end": v(3.03, -27.4) * mm});
            skLineSegment(sketch, "E273", {"start": v(-27, 5.59) * mm, "end": v(-27.59, 5.84) * mm});
            skLineSegment(sketch, "E274", {"start": v(-27.59, 5.84) * mm, "end": v(-28.14, 6.14) * mm});
            skLineSegment(sketch, "E275", {"start": v(-28.14, 6.14) * mm, "end": v(-28.68, 6.48) * mm});
            skLineSegment(sketch, "E276", {"start": v(-28.68, 6.48) * mm, "end": v(-29.2, 6.85) * mm});
            skLineSegment(sketch, "E277", {"start": v(-29.2, 6.85) * mm, "end": v(-29.69, 7.25) * mm});
            skLineSegment(sketch, "E278", {"start": v(-29.69, 7.25) * mm, "end": v(-30.16, 7.67) * mm});
            skLineSegment(sketch, "E279", {"start": v(-30.16, 7.67) * mm, "end": v(-30.62, 8.11) * mm});
            skLineSegment(sketch, "E280", {"start": v(-30.62, 8.11) * mm, "end": v(-31.05, 8.57) * mm});
            skLineSegment(sketch, "E281", {"start": v(-31.05, 8.57) * mm, "end": v(-31.47, 9.05) * mm});
            skLineSegment(sketch, "E282", {"start": v(-31.47, 9.05) * mm, "end": v(-31.88, 9.54) * mm});
            skLineSegment(sketch, "E283", {"start": v(-27.4, -3.03) * mm, "end": v(-28.04, -2.97) * mm});
            skLineSegment(sketch, "E284", {"start": v(-28.04, -2.97) * mm, "end": v(-28.66, -2.86) * mm});
            skLineSegment(sketch, "E285", {"start": v(-28.66, -2.86) * mm, "end": v(-29.28, -2.7) * mm});
            skLineSegment(sketch, "E286", {"start": v(-29.28, -2.7) * mm, "end": v(-29.88, -2.5) * mm});
            skLineSegment(sketch, "E287", {"start": v(-29.88, -2.5) * mm, "end": v(-30.47, -2.28) * mm});
            skLineSegment(sketch, "E288", {"start": v(-30.47, -2.28) * mm, "end": v(-31.05, -2.02) * mm});
            skLineSegment(sketch, "E289", {"start": v(-31.05, -2.02) * mm, "end": v(-31.62, -1.74) * mm});
            skLineSegment(sketch, "E290", {"start": v(-31.62, -1.74) * mm, "end": v(-32.18, -1.44) * mm});
            skLineSegment(sketch, "E291", {"start": v(-32.18, -1.44) * mm, "end": v(-32.73, -1.12) * mm});
            skLineSegment(sketch, "E292", {"start": v(-32.73, -1.12) * mm, "end": v(-33.26, -0.78) * mm});
            skLineSegment(sketch, "E293", {"start": v(-25.13, -11.35) * mm, "end": v(-25.75, -11.5) * mm});
            skLineSegment(sketch, "E294", {"start": v(-25.75, -11.5) * mm, "end": v(-26.38, -11.58) * mm});
            skLineSegment(sketch, "E295", {"start": v(-26.38, -11.58) * mm, "end": v(-27.01, -11.61) * mm});
            skLineSegment(sketch, "E296", {"start": v(-27.01, -11.61) * mm, "end": v(-27.64, -11.61) * mm});
            skLineSegment(sketch, "E297", {"start": v(-27.64, -11.61) * mm, "end": v(-28.28, -11.58) * mm});
            skLineSegment(sketch, "E298", {"start": v(-28.28, -11.58) * mm, "end": v(-28.9, -11.52) * mm});
            skLineSegment(sketch, "E299", {"start": v(-28.9, -11.52) * mm, "end": v(-29.54, -11.43) * mm});
            skLineSegment(sketch, "E300", {"start": v(-29.54, -11.43) * mm, "end": v(-30.16, -11.32) * mm});
            skLineSegment(sketch, "E301", {"start": v(-30.16, -11.32) * mm, "end": v(-30.78, -11.18) * mm});
            skLineSegment(sketch, "E302", {"start": v(-30.78, -11.18) * mm, "end": v(-31.4, -11.02) * mm});
            skLineSegment(sketch, "E303", {"start": v(-20.4, -18.56) * mm, "end": v(-20.94, -18.89) * mm});
            skLineSegment(sketch, "E304", {"start": v(-20.94, -18.89) * mm, "end": v(-21.5, -19.16) * mm});
            skLineSegment(sketch, "E305", {"start": v(-21.5, -19.16) * mm, "end": v(-22.1, -19.4) * mm});
            skLineSegment(sketch, "E306", {"start": v(-22.1, -19.4) * mm, "end": v(-22.7, -19.59) * mm});
            skLineSegment(sketch, "E307", {"start": v(-22.7, -19.59) * mm, "end": v(-23.32, -19.75) * mm});
            skLineSegment(sketch, "E308", {"start": v(-23.32, -19.75) * mm, "end": v(-23.93, -19.89) * mm});
            skLineSegment(sketch, "E309", {"start": v(-23.93, -19.89) * mm, "end": v(-24.56, -20) * mm});
            skLineSegment(sketch, "E310", {"start": v(-24.56, -20) * mm, "end": v(-25.19, -20.08) * mm});
            skLineSegment(sketch, "E311", {"start": v(-25.19, -20.08) * mm, "end": v(-25.82, -20.15) * mm});
            skLineSegment(sketch, "E312", {"start": v(-25.82, -20.15) * mm, "end": v(-26.45, -20.19) * mm});
            skArc(sketch, "E313", {"start": v(11.98, -23.66) * mm, "mid": v(11.4, -24.28) * mm, "end": v(11.35, -25.13) * mm});
            skArc(sketch, "E314", {"start": v(18.7, -18.8) * mm, "mid": v(18.35, -19.57) * mm, "end": v(18.56, -20.4) * mm});
            skArc(sketch, "E315", {"start": v(23.6, -12.1) * mm, "mid": v(23.5, -12.94) * mm, "end": v(23.96, -13.66) * mm});
            skArc(sketch, "E316", {"start": v(26.19, -4.22) * mm, "mid": v(26.35, -5.05) * mm, "end": v(27, -5.59) * mm});
            skLineSegment(sketch, "E317", {"start": v(-13.66, -23.96) * mm, "end": v(-14.08, -24.43) * mm});
            skLineSegment(sketch, "E318", {"start": v(-14.08, -24.43) * mm, "end": v(-14.54, -24.87) * mm});
            skLineSegment(sketch, "E319", {"start": v(-14.54, -24.87) * mm, "end": v(-15.03, -25.27) * mm});
            skLineSegment(sketch, "E320", {"start": v(-15.03, -25.27) * mm, "end": v(-15.54, -25.65) * mm});
            skLineSegment(sketch, "E321", {"start": v(-15.54, -25.65) * mm, "end": v(-16.07, -26) * mm});
            skLineSegment(sketch, "E322", {"start": v(-16.07, -26) * mm, "end": v(-16.62, -26.31) * mm});
            skLineSegment(sketch, "E323", {"start": v(-16.62, -26.31) * mm, "end": v(-17.18, -26.61) * mm});
            skLineSegment(sketch, "E324", {"start": v(-17.18, -26.61) * mm, "end": v(-17.75, -26.89) * mm});
            skLineSegment(sketch, "E325", {"start": v(-17.75, -26.89) * mm, "end": v(-18.33, -27.14) * mm});
            skLineSegment(sketch, "E326", {"start": v(-18.33, -27.14) * mm, "end": v(-18.92, -27.37) * mm});
            skLineSegment(sketch, "E327", {"start": v(-5.59, -27) * mm, "end": v(-5.84, -27.59) * mm});
            skLineSegment(sketch, "E328", {"start": v(-5.84, -27.59) * mm, "end": v(-6.14, -28.14) * mm});
            skLineSegment(sketch, "E329", {"start": v(-6.14, -28.14) * mm, "end": v(-6.48, -28.68) * mm});
            skLineSegment(sketch, "E330", {"start": v(-6.48, -28.68) * mm, "end": v(-6.85, -29.2) * mm});
            skLineSegment(sketch, "E331", {"start": v(-6.85, -29.2) * mm, "end": v(-7.25, -29.69) * mm});
            skLineSegment(sketch, "E332", {"start": v(-7.25, -29.69) * mm, "end": v(-7.67, -30.16) * mm});
            skLineSegment(sketch, "E333", {"start": v(-7.67, -30.16) * mm, "end": v(-8.11, -30.62) * mm});
            skLineSegment(sketch, "E334", {"start": v(-8.11, -30.62) * mm, "end": v(-8.57, -31.05) * mm});
            skLineSegment(sketch, "E335", {"start": v(-8.57, -31.05) * mm, "end": v(-9.05, -31.47) * mm});
            skLineSegment(sketch, "E336", {"start": v(-9.05, -31.47) * mm, "end": v(-9.54, -31.88) * mm});
            skLineSegment(sketch, "E337", {"start": v(3.03, -27.4) * mm, "end": v(2.97, -28.04) * mm});
            skLineSegment(sketch, "E338", {"start": v(2.97, -28.04) * mm, "end": v(2.86, -28.66) * mm});
            skLineSegment(sketch, "E339", {"start": v(2.86, -28.66) * mm, "end": v(2.7, -29.28) * mm});
            skLineSegment(sketch, "E340", {"start": v(2.7, -29.28) * mm, "end": v(2.5, -29.88) * mm});
            skLineSegment(sketch, "E341", {"start": v(2.5, -29.88) * mm, "end": v(2.28, -30.47) * mm});
            skLineSegment(sketch, "E342", {"start": v(2.28, -30.47) * mm, "end": v(2.02, -31.05) * mm});
            skLineSegment(sketch, "E343", {"start": v(2.02, -31.05) * mm, "end": v(1.74, -31.62) * mm});
            skLineSegment(sketch, "E344", {"start": v(1.74, -31.62) * mm, "end": v(1.44, -32.18) * mm});
            skLineSegment(sketch, "E345", {"start": v(1.44, -32.18) * mm, "end": v(1.12, -32.73) * mm});
            skLineSegment(sketch, "E346", {"start": v(1.12, -32.73) * mm, "end": v(0.78, -33.26) * mm});
            skLineSegment(sketch, "E347", {"start": v(11.35, -25.13) * mm, "end": v(11.5, -25.75) * mm});
            skLineSegment(sketch, "E348", {"start": v(11.5, -25.75) * mm, "end": v(11.58, -26.38) * mm});
            skLineSegment(sketch, "E349", {"start": v(11.58, -26.38) * mm, "end": v(11.61, -27.01) * mm});
            skLineSegment(sketch, "E350", {"start": v(11.61, -27.01) * mm, "end": v(11.61, -27.64) * mm});
            skLineSegment(sketch, "E351", {"start": v(11.61, -27.64) * mm, "end": v(11.58, -28.28) * mm});
            skLineSegment(sketch, "E352", {"start": v(11.58, -28.28) * mm, "end": v(11.52, -28.9) * mm});
            skLineSegment(sketch, "E353", {"start": v(11.52, -28.9) * mm, "end": v(11.43, -29.54) * mm});
            skLineSegment(sketch, "E354", {"start": v(11.43, -29.54) * mm, "end": v(11.32, -30.16) * mm});
            skLineSegment(sketch, "E355", {"start": v(11.32, -30.16) * mm, "end": v(11.18, -30.78) * mm});
            skLineSegment(sketch, "E356", {"start": v(11.18, -30.78) * mm, "end": v(11.02, -31.4) * mm});
            skArc(sketch, "E357", {"start": v(26.2, 4.08) * mm, "mid": v(26.62, 3.34) * mm, "end": v(27.4, 3.03) * mm});
            skArc(sketch, "E358", {"start": v(23.66, 11.98) * mm, "mid": v(24.28, 11.4) * mm, "end": v(25.13, 11.35) * mm});
            skArc(sketch, "E359", {"start": v(18.8, 18.7) * mm, "mid": v(19.57, 18.35) * mm, "end": v(20.4, 18.56) * mm});
            skArc(sketch, "E360", {"start": v(12.1, 23.6) * mm, "mid": v(12.94, 23.5) * mm, "end": v(13.66, 23.96) * mm});
            skLineSegment(sketch, "E361", {"start": v(18.56, -20.4) * mm, "end": v(18.89, -20.94) * mm});
            skLineSegment(sketch, "E362", {"start": v(18.89, -20.94) * mm, "end": v(19.16, -21.5) * mm});
            skLineSegment(sketch, "E363", {"start": v(19.16, -21.5) * mm, "end": v(19.4, -22.1) * mm});
            skLineSegment(sketch, "E364", {"start": v(19.4, -22.1) * mm, "end": v(19.59, -22.7) * mm});
            skLineSegment(sketch, "E365", {"start": v(19.59, -22.7) * mm, "end": v(19.75, -23.32) * mm});
            skLineSegment(sketch, "E366", {"start": v(19.75, -23.32) * mm, "end": v(19.89, -23.93) * mm});
            skLineSegment(sketch, "E367", {"start": v(19.89, -23.93) * mm, "end": v(20, -24.56) * mm});
            skLineSegment(sketch, "E368", {"start": v(20, -24.56) * mm, "end": v(20.08, -25.19) * mm});
            skLineSegment(sketch, "E369", {"start": v(20.08, -25.19) * mm, "end": v(20.15, -25.82) * mm});
            skLineSegment(sketch, "E370", {"start": v(20.15, -25.82) * mm, "end": v(20.19, -26.45) * mm});
            skLineSegment(sketch, "E371", {"start": v(23.96, -13.66) * mm, "end": v(24.43, -14.08) * mm});
            skLineSegment(sketch, "E372", {"start": v(24.43, -14.08) * mm, "end": v(24.87, -14.54) * mm});
            skLineSegment(sketch, "E373", {"start": v(24.87, -14.54) * mm, "end": v(25.27, -15.03) * mm});
            skLineSegment(sketch, "E374", {"start": v(25.27, -15.03) * mm, "end": v(25.65, -15.54) * mm});
            skLineSegment(sketch, "E375", {"start": v(25.65, -15.54) * mm, "end": v(26, -16.07) * mm});
            skLineSegment(sketch, "E376", {"start": v(26, -16.07) * mm, "end": v(26.31, -16.62) * mm});
            skLineSegment(sketch, "E377", {"start": v(26.31, -16.62) * mm, "end": v(26.61, -17.18) * mm});
            skLineSegment(sketch, "E378", {"start": v(26.61, -17.18) * mm, "end": v(26.89, -17.75) * mm});
            skLineSegment(sketch, "E379", {"start": v(26.89, -17.75) * mm, "end": v(27.14, -18.33) * mm});
            skLineSegment(sketch, "E380", {"start": v(27.14, -18.33) * mm, "end": v(27.37, -18.92) * mm});
            skLineSegment(sketch, "E381", {"start": v(27, -5.59) * mm, "end": v(27.59, -5.84) * mm});
            skLineSegment(sketch, "E382", {"start": v(27.59, -5.84) * mm, "end": v(28.14, -6.14) * mm});
            skLineSegment(sketch, "E383", {"start": v(28.14, -6.14) * mm, "end": v(28.68, -6.48) * mm});
            skLineSegment(sketch, "E384", {"start": v(28.68, -6.48) * mm, "end": v(29.2, -6.85) * mm});
            skLineSegment(sketch, "E385", {"start": v(29.2, -6.85) * mm, "end": v(29.69, -7.25) * mm});
            skLineSegment(sketch, "E386", {"start": v(29.69, -7.25) * mm, "end": v(30.16, -7.67) * mm});
            skLineSegment(sketch, "E387", {"start": v(30.16, -7.67) * mm, "end": v(30.62, -8.11) * mm});
            skLineSegment(sketch, "E388", {"start": v(30.62, -8.11) * mm, "end": v(31.05, -8.57) * mm});
            skLineSegment(sketch, "E389", {"start": v(31.05, -8.57) * mm, "end": v(31.47, -9.05) * mm});
            skLineSegment(sketch, "E390", {"start": v(31.47, -9.05) * mm, "end": v(31.88, -9.54) * mm});
            skLineSegment(sketch, "E391", {"start": v(27.4, 3.03) * mm, "end": v(28.04, 2.97) * mm});
            skLineSegment(sketch, "E392", {"start": v(28.04, 2.97) * mm, "end": v(28.66, 2.86) * mm});
            skLineSegment(sketch, "E393", {"start": v(28.66, 2.86) * mm, "end": v(29.28, 2.7) * mm});
            skLineSegment(sketch, "E394", {"start": v(29.28, 2.7) * mm, "end": v(29.88, 2.5) * mm});
            skLineSegment(sketch, "E395", {"start": v(29.88, 2.5) * mm, "end": v(30.47, 2.28) * mm});
            skLineSegment(sketch, "E396", {"start": v(30.47, 2.28) * mm, "end": v(31.05, 2.02) * mm});
            skLineSegment(sketch, "E397", {"start": v(31.05, 2.02) * mm, "end": v(31.62, 1.74) * mm});
            skLineSegment(sketch, "E398", {"start": v(31.62, 1.74) * mm, "end": v(32.18, 1.44) * mm});
            skLineSegment(sketch, "E399", {"start": v(32.18, 1.44) * mm, "end": v(32.73, 1.12) * mm});
            skLineSegment(sketch, "E400", {"start": v(32.73, 1.12) * mm, "end": v(33.26, 0.78) * mm});
            skArc(sketch, "E401", {"start": v(4.22, 26.19) * mm, "mid": v(5.05, 26.35) * mm, "end": v(5.59, 27) * mm});
            skArc(sketch, "E402", {"start": v(-5.59, 27) * mm, "mid": v(-5.05, 26.35) * mm, "end": v(-4.22, 26.19) * mm});
            skArc(sketch, "E403", {"start": v(-13.66, 23.96) * mm, "mid": v(-12.94, 23.5) * mm, "end": v(-12.1, 23.6) * mm});
            skArc(sketch, "E404", {"start": v(-20.4, 18.56) * mm, "mid": v(-19.57, 18.35) * mm, "end": v(-18.8, 18.7) * mm});
            skLineSegment(sketch, "E405", {"start": v(25.13, 11.35) * mm, "end": v(25.75, 11.5) * mm});
            skLineSegment(sketch, "E406", {"start": v(25.75, 11.5) * mm, "end": v(26.38, 11.58) * mm});
            skLineSegment(sketch, "E407", {"start": v(26.38, 11.58) * mm, "end": v(27.01, 11.61) * mm});
            skLineSegment(sketch, "E408", {"start": v(27.01, 11.61) * mm, "end": v(27.64, 11.61) * mm});
            skLineSegment(sketch, "E409", {"start": v(27.64, 11.61) * mm, "end": v(28.28, 11.58) * mm});
            skLineSegment(sketch, "E410", {"start": v(28.28, 11.58) * mm, "end": v(28.9, 11.52) * mm});
            skLineSegment(sketch, "E411", {"start": v(28.9, 11.52) * mm, "end": v(29.54, 11.43) * mm});
            skLineSegment(sketch, "E412", {"start": v(29.54, 11.43) * mm, "end": v(30.16, 11.32) * mm});
            skLineSegment(sketch, "E413", {"start": v(30.16, 11.32) * mm, "end": v(30.78, 11.18) * mm});
            skLineSegment(sketch, "E414", {"start": v(30.78, 11.18) * mm, "end": v(31.4, 11.02) * mm});
            skLineSegment(sketch, "E415", {"start": v(20.4, 18.56) * mm, "end": v(20.94, 18.89) * mm});
            skLineSegment(sketch, "E416", {"start": v(20.94, 18.89) * mm, "end": v(21.5, 19.16) * mm});
            skLineSegment(sketch, "E417", {"start": v(21.5, 19.16) * mm, "end": v(22.1, 19.4) * mm});
            skLineSegment(sketch, "E418", {"start": v(22.1, 19.4) * mm, "end": v(22.7, 19.59) * mm});
            skLineSegment(sketch, "E419", {"start": v(22.7, 19.59) * mm, "end": v(23.32, 19.75) * mm});
            skLineSegment(sketch, "E420", {"start": v(23.32, 19.75) * mm, "end": v(23.93, 19.89) * mm});
            skLineSegment(sketch, "E421", {"start": v(23.93, 19.89) * mm, "end": v(24.56, 20) * mm});
            skLineSegment(sketch, "E422", {"start": v(24.56, 20) * mm, "end": v(25.19, 20.08) * mm});
            skLineSegment(sketch, "E423", {"start": v(25.19, 20.08) * mm, "end": v(25.82, 20.15) * mm});
            skLineSegment(sketch, "E424", {"start": v(25.82, 20.15) * mm, "end": v(26.45, 20.19) * mm});
            skLineSegment(sketch, "E425", {"start": v(13.66, 23.96) * mm, "end": v(14.08, 24.43) * mm});
            skLineSegment(sketch, "E426", {"start": v(14.08, 24.43) * mm, "end": v(14.54, 24.87) * mm});
            skLineSegment(sketch, "E427", {"start": v(14.54, 24.87) * mm, "end": v(15.03, 25.27) * mm});
            skLineSegment(sketch, "E428", {"start": v(15.03, 25.27) * mm, "end": v(15.54, 25.65) * mm});
            skLineSegment(sketch, "E429", {"start": v(15.54, 25.65) * mm, "end": v(16.07, 26) * mm});
            skLineSegment(sketch, "E430", {"start": v(16.07, 26) * mm, "end": v(16.62, 26.31) * mm});
            skLineSegment(sketch, "E431", {"start": v(16.62, 26.31) * mm, "end": v(17.18, 26.61) * mm});
            skLineSegment(sketch, "E432", {"start": v(17.18, 26.61) * mm, "end": v(17.75, 26.89) * mm});
            skLineSegment(sketch, "E433", {"start": v(17.75, 26.89) * mm, "end": v(18.33, 27.14) * mm});
            skLineSegment(sketch, "E434", {"start": v(18.33, 27.14) * mm, "end": v(18.92, 27.37) * mm});
            skLineSegment(sketch, "E435", {"start": v(5.59, 27) * mm, "end": v(5.84, 27.59) * mm});
            skLineSegment(sketch, "E436", {"start": v(5.84, 27.59) * mm, "end": v(6.14, 28.14) * mm});
            skLineSegment(sketch, "E437", {"start": v(6.14, 28.14) * mm, "end": v(6.48, 28.68) * mm});
            skLineSegment(sketch, "E438", {"start": v(6.48, 28.68) * mm, "end": v(6.85, 29.2) * mm});
            skLineSegment(sketch, "E439", {"start": v(6.85, 29.2) * mm, "end": v(7.25, 29.69) * mm});
            skLineSegment(sketch, "E440", {"start": v(7.25, 29.69) * mm, "end": v(7.67, 30.16) * mm});
            skLineSegment(sketch, "E441", {"start": v(7.67, 30.16) * mm, "end": v(8.11, 30.62) * mm});
            skLineSegment(sketch, "E442", {"start": v(8.11, 30.62) * mm, "end": v(8.57, 31.05) * mm});
            skLineSegment(sketch, "E443", {"start": v(8.57, 31.05) * mm, "end": v(9.05, 31.47) * mm});
            skLineSegment(sketch, "E444", {"start": v(9.05, 31.47) * mm, "end": v(9.54, 31.88) * mm});
            skArc(sketch, "E445", {"start": v(-25.13, 11.35) * mm, "mid": v(-24.28, 11.4) * mm, "end": v(-23.66, 11.98) * mm});
            skArc(sketch, "E446", {"start": v(-27.4, 3.03) * mm, "mid": v(-26.62, 3.34) * mm, "end": v(-26.2, 4.08) * mm});
            skArc(sketch, "E447", {"start": v(-27, -5.59) * mm, "mid": v(-26.35, -5.05) * mm, "end": v(-26.19, -4.22) * mm});
            skArc(sketch, "E448", {"start": v(-23.96, -13.66) * mm, "mid": v(-23.5, -12.94) * mm, "end": v(-23.6, -12.1) * mm});
            skArc(sketch, "E449", {"start": v(-18.56, -20.4) * mm, "mid": v(-18.35, -19.57) * mm, "end": v(-18.7, -18.8) * mm});
            skArc(sketch, "E450", {"start": v(-11.35, -25.13) * mm, "mid": v(-11.4, -24.28) * mm, "end": v(-11.98, -23.66) * mm});
            skArc(sketch, "E451", {"start": v(-3.03, -27.4) * mm, "mid": v(-3.34, -26.62) * mm, "end": v(-4.08, -26.2) * mm});
            skArc(sketch, "E452", {"start": v(5.59, -27) * mm, "mid": v(5.05, -26.35) * mm, "end": v(4.22, -26.19) * mm});
            skArc(sketch, "E453", {"start": v(13.66, -23.96) * mm, "mid": v(12.94, -23.5) * mm, "end": v(12.1, -23.6) * mm});
            skArc(sketch, "E454", {"start": v(20.4, -18.56) * mm, "mid": v(19.57, -18.35) * mm, "end": v(18.8, -18.7) * mm});
            skArc(sketch, "E455", {"start": v(25.13, -11.35) * mm, "mid": v(24.28, -11.4) * mm, "end": v(23.66, -11.98) * mm});
            skArc(sketch, "E456", {"start": v(27.4, -3.03) * mm, "mid": v(26.62, -3.34) * mm, "end": v(26.2, -4.08) * mm});
            skArc(sketch, "E457", {"start": v(27, 5.59) * mm, "mid": v(26.35, 5.05) * mm, "end": v(26.19, 4.22) * mm});
            skArc(sketch, "E458", {"start": v(23.96, 13.66) * mm, "mid": v(23.5, 12.94) * mm, "end": v(23.6, 12.1) * mm});
            skArc(sketch, "E459", {"start": v(18.56, 20.4) * mm, "mid": v(18.35, 19.57) * mm, "end": v(18.7, 18.8) * mm});
            skArc(sketch, "E460", {"start": v(11.35, 25.13) * mm, "mid": v(11.4, 24.28) * mm, "end": v(11.98, 23.66) * mm});
            skArc(sketch, "E461", {"start": v(-9.54, 31.88) * mm, "mid": v(-10.28, 31.65) * mm, "end": v(-11.02, 31.4) * mm});
            skArc(sketch, "E462", {"start": v(-18.92, 27.37) * mm, "mid": v(-19.56, 26.92) * mm, "end": v(-20.19, 26.45) * mm});
            skArc(sketch, "E463", {"start": v(-26.45, 20.19) * mm, "mid": v(-26.92, 19.56) * mm, "end": v(-27.37, 18.92) * mm});
            skArc(sketch, "E464", {"start": v(-31.4, 11.02) * mm, "mid": v(-31.65, 10.28) * mm, "end": v(-31.88, 9.54) * mm});
            skArc(sketch, "E465", {"start": v(-33.26, 0.78) * mm, "mid": v(-33.27, 0) * mm, "end": v(-33.26, -0.78) * mm});
            skArc(sketch, "E466", {"start": v(-31.88, -9.54) * mm, "mid": v(-31.65, -10.28) * mm, "end": v(-31.4, -11.02) * mm});
            skArc(sketch, "E467", {"start": v(-27.37, -18.92) * mm, "mid": v(-26.92, -19.56) * mm, "end": v(-26.45, -20.19) * mm});
            skArc(sketch, "E468", {"start": v(-20.19, -26.45) * mm, "mid": v(-19.56, -26.92) * mm, "end": v(-18.92, -27.37) * mm});
            skArc(sketch, "E469", {"start": v(-11.02, -31.4) * mm, "mid": v(-10.28, -31.65) * mm, "end": v(-9.54, -31.88) * mm});
            skArc(sketch, "E470", {"start": v(-0.78, -33.26) * mm, "mid": v(0, -33.27) * mm, "end": v(0.78, -33.26) * mm});
            skArc(sketch, "E471", {"start": v(9.54, -31.88) * mm, "mid": v(10.28, -31.65) * mm, "end": v(11.02, -31.4) * mm});
            skArc(sketch, "E472", {"start": v(18.92, -27.37) * mm, "mid": v(19.56, -26.92) * mm, "end": v(20.19, -26.45) * mm});
            skArc(sketch, "E473", {"start": v(26.45, -20.19) * mm, "mid": v(26.92, -19.56) * mm, "end": v(27.37, -18.92) * mm});
            skArc(sketch, "E474", {"start": v(31.4, -11.02) * mm, "mid": v(31.65, -10.28) * mm, "end": v(31.88, -9.54) * mm});
            skArc(sketch, "E475", {"start": v(33.26, -0.78) * mm, "mid": v(33.27, 0) * mm, "end": v(33.26, 0.78) * mm});
            skArc(sketch, "E476", {"start": v(31.88, 9.54) * mm, "mid": v(31.65, 10.28) * mm, "end": v(31.4, 11.02) * mm});
            skArc(sketch, "E477", {"start": v(27.37, 18.92) * mm, "mid": v(26.92, 19.56) * mm, "end": v(26.45, 20.19) * mm});
            skArc(sketch, "E478", {"start": v(20.19, 26.45) * mm, "mid": v(19.56, 26.92) * mm, "end": v(18.92, 27.37) * mm});
            skArc(sketch, "E479", {"start": v(11.02, 31.4) * mm, "mid": v(10.28, 31.65) * mm, "end": v(9.54, 31.88) * mm});
            skSolve(sketch);
        }
        {
            var Q0;
            Q0 = qSketchRegion(id + "F0", true);
            extrude(context, id + "F1", {"entities" : qUnion([Q0]), "depth" : 12.7 * mm, "offsetDistance" : 25.4 * mm});
        }
    });
